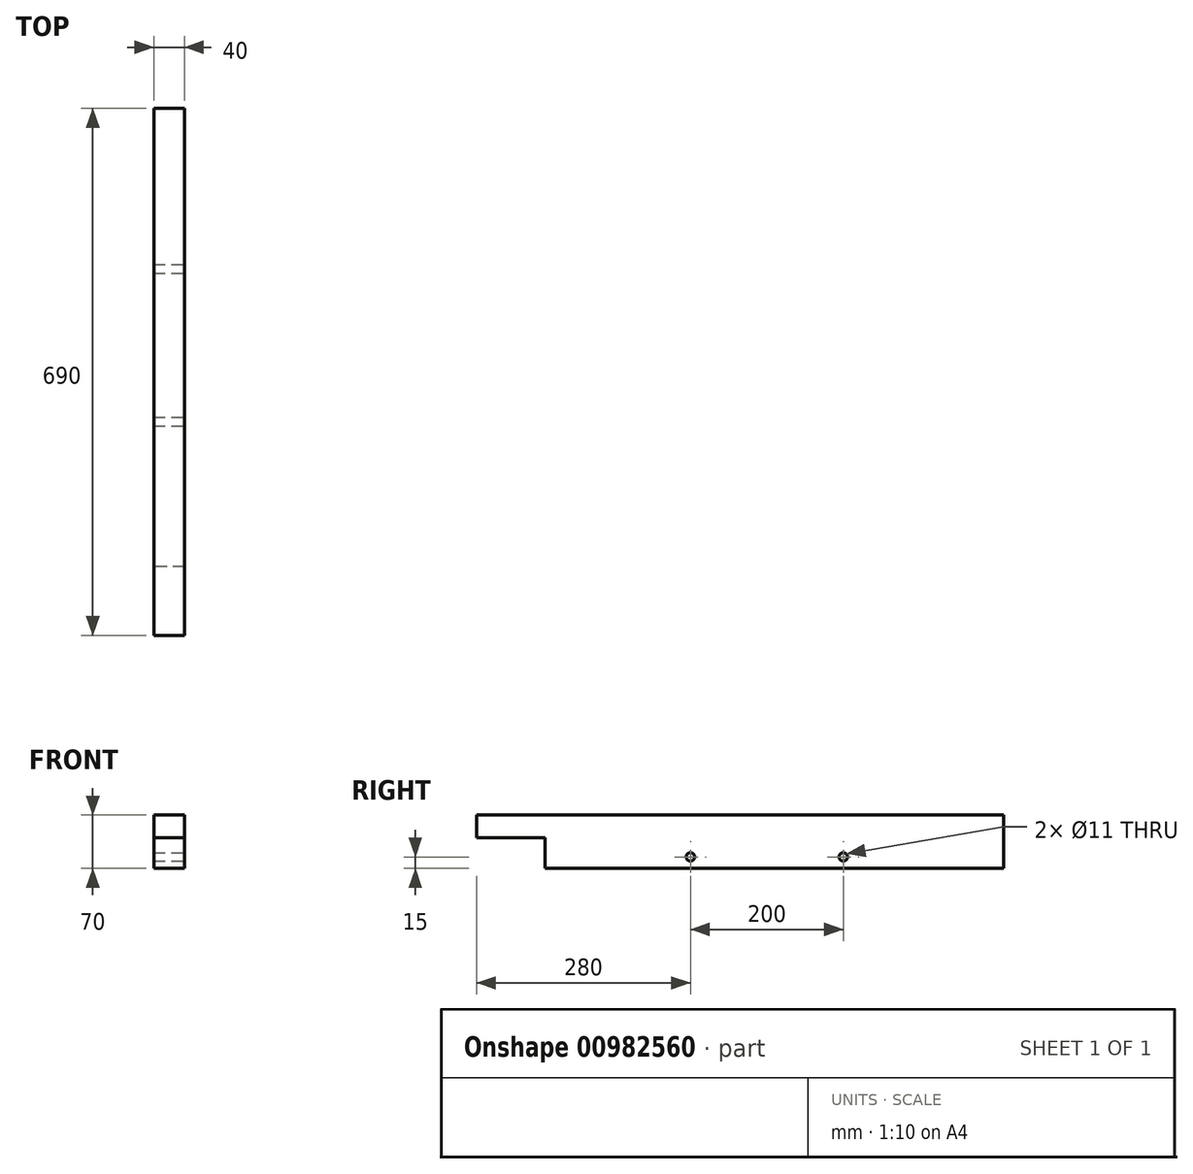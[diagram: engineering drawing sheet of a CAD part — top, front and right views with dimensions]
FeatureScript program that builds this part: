
annotation { "Feature Type Name" : "Feature", "Feature Type Description" : "" }
export const myFeature = defineFeature(function(context is Context, id is Id, definition is map)
    precondition{}
    {
        {
            var Q0;
            Q0=qCreatedBy(makeId("Front.planeOp"),FACE);
            var sketch = newSketch(context, id + "F0", { "sketchPlane" : qUnion([Q0])});
            skLineSegment(sketch, "E0", {"start": v(0, 0) * mm, "end": v(0, 70) * mm});
            skLineSegment(sketch, "E1", {"start": v(0, 70) * mm, "end": v(40, 70) * mm});
            skLineSegment(sketch, "E2", {"start": v(40, 70) * mm, "end": v(40, 0) * mm});
            skLineSegment(sketch, "E3", {"start": v(40, 0) * mm, "end": v(0, 0) * mm});
            skSolve(sketch);
        }
        {
            var Q0;
            Q0=makeQuery(id+"F0.imprint","IMPRINT",FACE,{"disambiguationData":[TD([[makeQuery(id+"F0.imprint","IMPRINT",EDGE,{"derivedFrom":sQuery(id+"F0.wireOp",EDGE,"E0")}),-1.0]])]});
            extrude(context, id + "F1", {"entities" : qUnion([Q0]), "depth" : 600 * mm, "offsetDistance" : 25 * mm});
        }
        {
            var Q0;
            Q0=makeQuery(id+"F1.opExtrude","SWEPT_FACE",FACE,{"disambiguationData":[OSD([sQuery(id+"F0.wireOp",EDGE,"E2")])]});
            var sketch = newSketch(context, id + "F2", { "sketchPlane" : qUnion([Q0])});
            skPoint(sketch, "E4", {"position": v(-410, 15) * mm});
            skPoint(sketch, "E5", {"position": v(-210, 15) * mm});
            skSolve(sketch);
        }
        {
            var Q0;
            Q0=sQuery(id+"F2.wireOp",VERTEX,"E4");
            var Q1;
            Q1=sQuery(id+"F2.wireOp",VERTEX,"E5");
            var Q2;
            Q2=makeQuery(id+"F1.opExtrude","SWEPT_BODY",BODY,{"disambiguationData":[OSD([sQuery(id+"F0.wireOp",EDGE,"E0"),sQuery(id+"F0.wireOp",EDGE,"E1"),sQuery(id+"F0.wireOp",EDGE,"E2"),sQuery(id+"F0.wireOp",EDGE,"E3")])]});
            hole(context, id + "F3", {"style" : HoleStyle.SIMPLE, "endStyle" : HoleEndStyle.BLIND, "holeDiameter" : 11 * mm, "majorDiameter" : 5 * mm, "holeDepth" : 50 * mm, "isTappedThrough" : true, "tappedDepth" : 4 * mm, "tapClearance" : 3, "startFromSketch" : true, "locations" : qUnion([Q0, Q1]), "scope" : qUnion([Q2])});
        }
        {
            var Q0;
            Q0=makeQuery(id+"F1.opExtrude","CAP_FACE",FACE,{"disambiguationData":[OSD([sQuery(id+"F0.wireOp",EDGE,"E0"),sQuery(id+"F0.wireOp",EDGE,"E1"),sQuery(id+"F0.wireOp",EDGE,"E2"),sQuery(id+"F0.wireOp",EDGE,"E3")])],"isStart":false});
            var sketch = newSketch(context, id + "F4", { "sketchPlane" : qUnion([Q0])});
            skLineSegment(sketch, "E6.bottom", {"start": v(0, 70) * mm, "end": v(40, 70) * mm});
            skLineSegment(sketch, "E6.top", {"start": v(0, 40) * mm, "end": v(40, 40) * mm});
            skLineSegment(sketch, "E6.left", {"start": v(0, 70) * mm, "end": v(0, 40) * mm});
            skLineSegment(sketch, "E6.right", {"start": v(40, 70) * mm, "end": v(40, 40) * mm});
            skSolve(sketch);
        }
        {
            var Q0;
            Q0 = qSketchRegion(id + "F4", true);
            extrude(context, id + "F5", {"entities" : qUnion([Q0]), "operationType" : NewBodyOperationType.ADD, "depth" : 90 * mm, "offsetDistance" : 25 * mm});
        }
    });
